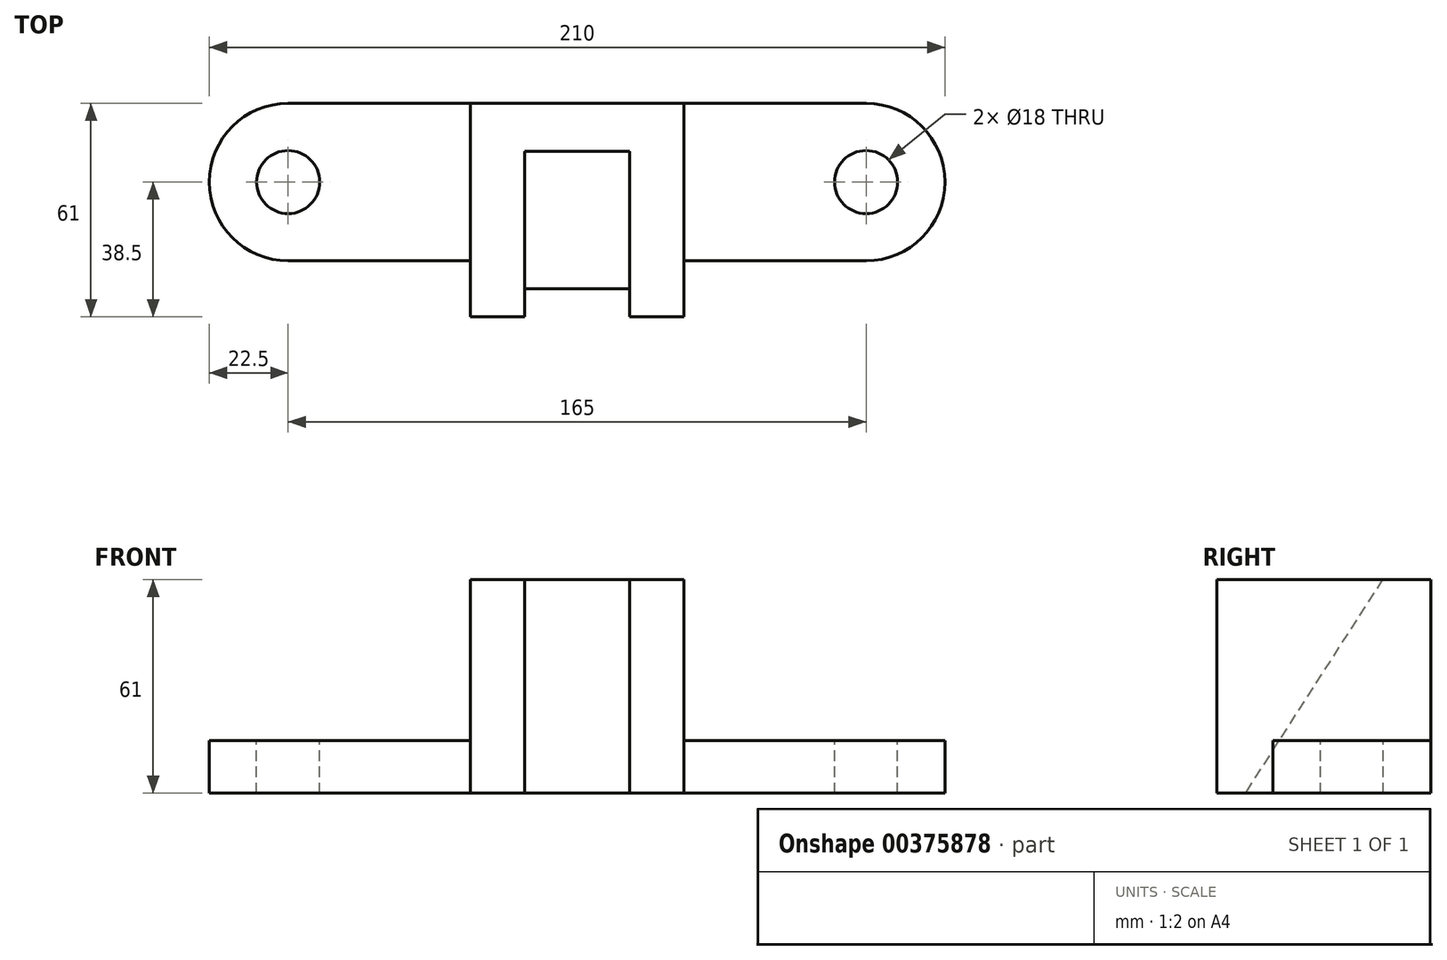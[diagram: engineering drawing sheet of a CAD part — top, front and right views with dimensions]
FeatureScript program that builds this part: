
annotation { "Feature Type Name" : "Feature", "Feature Type Description" : "" }
export const myFeature = defineFeature(function(context is Context, id is Id, definition is map)
    precondition{}
    {
        {
            var Q0;
            Q0=qCreatedBy(makeId("Front.planeOp"),FACE);
            var sketch = newSketch(context, id + "F0", { "sketchPlane" : qUnion([Q0])});
            skLineSegment(sketch, "E0.bottom", {"start": v(-30.5, 30.5) * mm, "end": v(30.5, 30.5) * mm});
            skLineSegment(sketch, "E0.top", {"start": v(-30.5, -30.5) * mm, "end": v(30.5, -30.5) * mm});
            skLineSegment(sketch, "E0.left", {"start": v(-30.5, 30.5) * mm, "end": v(-30.5, -30.5) * mm});
            skLineSegment(sketch, "E0.right", {"start": v(30.5, 30.5) * mm, "end": v(30.5, -30.5) * mm});
            skLineSegment(sketch, "E1.bottom", {"start": v(-30.5, -30.5) * mm, "end": v(-82.5, -30.5) * mm});
            skLineSegment(sketch, "E1.top", {"start": v(-30.5, -15.5) * mm, "end": v(-82.5, -15.5) * mm});
            skLineSegment(sketch, "E1.left", {"start": v(-30.5, -30.5) * mm, "end": v(-30.5, -15.5) * mm});
            skLineSegment(sketch, "E1.right", {"start": v(-82.5, -30.5) * mm, "end": v(-82.5, -15.5) * mm});
            skLineSegment(sketch, "E2.bottom", {"start": v(30.5, -30.5) * mm, "end": v(82.5, -30.5) * mm});
            skLineSegment(sketch, "E2.top", {"start": v(30.5, -15.5) * mm, "end": v(82.5, -15.5) * mm});
            skLineSegment(sketch, "E2.left", {"start": v(30.5, -30.5) * mm, "end": v(30.5, -15.5) * mm});
            skLineSegment(sketch, "E2.right", {"start": v(82.5, -30.5) * mm, "end": v(82.5, -15.5) * mm});
            skSolve(sketch);
        }
        {
            var Q0;
            Q0=makeQuery(id+"F0.imprint","IMPRINT",FACE,{"disambiguationData":[TD([[makeQuery(id+"F0.imprint","IMPRINT",EDGE,{"derivedFrom":sQuery(id+"F0.wireOp",EDGE,"E1.bottom")}),-1.0]])]});
            var Q1;
            Q1=makeQuery(id+"F0.imprint","IMPRINT",FACE,{"disambiguationData":[TD([[makeQuery(id+"F0.imprint","IMPRINT",EDGE,{"derivedFrom":sQuery(id+"F0.wireOp",EDGE,"E2.bottom")}),1.0]])]});
            extrude(context, id + "F1", {"entities" : qUnion([Q0, Q1]), "depth" : 45 * mm});
        }
        {
            var Q0;
            Q0=makeQuery(id+"F0.imprint","IMPRINT",FACE,{"disambiguationData":[TD([[makeQuery(id+"F0.imprint","IMPRINT",EDGE,{"derivedFrom":sQuery(id+"F0.wireOp",EDGE,"E0.bottom")}),-1.0]])]});
            extrude(context, id + "F2", {"entities" : qUnion([Q0]), "operationType" : NewBodyOperationType.ADD, "depth" : 61 * mm});
        }
        {
            var Q0;
            Q0=makeQuery(id+"F1.opExtrude","SWEPT_FACE",FACE,{"disambiguationData":[OSD([sQuery(id+"F0.wireOp",EDGE,"E1.top")])]});
            var sketch = newSketch(context, id + "F3", { "sketchPlane" : qUnion([Q0])});
            skCircle(sketch, "E3", {"center": v(-82.5, -22.5) * mm, "radius": 22.5 * mm});
            skLineSegment(sketch, "E4", {"start": v(-82.5, 0) * mm, "end": v(-82.5, -45) * mm});
            skArc(sketch, "E5", {"start": v(82.5, -45) * mm, "mid": v(105, -22.5) * mm, "end": v(82.5, 0) * mm});
            skLineSegment(sketch, "E6", {"start": v(82.5, 0) * mm, "end": v(82.5, -45) * mm});
            skSolve(sketch);
        }
        {
            var Q0;
            {var subQ0=sQuery(id+"F3.wireOp",EDGE,"E4");Q0=makeQuery(id+"F3.imprint","IMPRINT",FACE,{"disambiguationData":[TD([[makeQuery(id+"F3.imprint","IMPRINT",EDGE,{"derivedFrom":subQ0}),1.0]])]});}
            var Q1;
            Q1=makeQuery(id+"F3.imprint","IMPRINT",FACE,{"disambiguationData":[TD([[makeQuery(id+"F3.imprint","IMPRINT",EDGE,{"derivedFrom":sQuery(id+"F3.wireOp",EDGE,"E5")}),1.0]])]});
            extrude(context, id + "F4", {"entities" : qUnion([Q0, Q1]), "operationType" : NewBodyOperationType.ADD, "oppositeDirection" : true, "depth" : 15 * mm});
        }
        {
            var Q0;
            Q0=makeQuery(id+"F4.opExtrude","CAP_FACE",FACE,{"disambiguationData":[OSD([sQuery(id+"F3.wireOp",EDGE,"E3"),sQuery(id+"F3.wireOp",EDGE,"E4")])],"isStart":true});
            var sketch = newSketch(context, id + "F5", { "sketchPlane" : qUnion([Q0])});
            skCircle(sketch, "E7", {"center": v(-82.5, -22.5) * mm, "radius": 9 * mm});
            skSolve(sketch);
        }
        {
            var Q0;
            Q0=makeQuery(id+"F4.opExtrude","CAP_FACE",FACE,{"disambiguationData":[OSD([sQuery(id+"F3.wireOp",EDGE,"E5"),sQuery(id+"F3.wireOp",EDGE,"E6")])],"isStart":true});
            var sketch = newSketch(context, id + "F6", { "sketchPlane" : qUnion([Q0])});
            skCircle(sketch, "E8", {"center": v(82.5, -22.5) * mm, "radius": 9 * mm});
            skSolve(sketch);
        }
        {
            var Q0;
            Q0=makeQuery(id+"F6.imprint","IMPRINT",FACE,{"disambiguationData":[TD([[makeQuery(id+"F6.imprint","IMPRINT",EDGE,{"derivedFrom":sQuery(id+"F6.wireOp",EDGE,"E8")}),1.0]])]});
            var Q1;
            Q1=makeQuery(id+"F5.imprint","IMPRINT",FACE,{"disambiguationData":[TD([[makeQuery(id+"F5.imprint","IMPRINT",EDGE,{"derivedFrom":sQuery(id+"F5.wireOp",EDGE,"E7")}),1.0]])]});
            extrude(context, id + "F7", {"entities" : qUnion([Q0, Q1]), "operationType" : NewBodyOperationType.REMOVE, "oppositeDirection" : true, "depth" : 15 * mm});
        }
        {
            var Q0;
            Q0=makeQuery(id+"F2.opExtrude","SWEPT_FACE",FACE,{"disambiguationData":[OSD([sQuery(id+"F0.wireOp",EDGE,"E0.left"),sQuery(id+"F0.wireOp",EDGE,"E1.left")])]});
            cPlane(context, id + "F8", {"entities" : qUnion([Q0]), "cplaneType" : CPlaneType.OFFSET, "offset" : 15.5 * mm, "oppositeDirection" : true, "width" : 150 * mm, "height" : 150 * mm});
        }
        {
            var Q0;
            Q0=qCreatedBy(id+"F8.planeOp",FACE);
            var sketch = newSketch(context, id + "F9", { "sketchPlane" : qUnion([Q0])});
            skLineSegment(sketch, "E9", {"start": v(13.75, 30.5) * mm, "end": v(53, -30.5) * mm});
            skLineSegment(sketch, "E10", {"start": v(13.75, 30.5) * mm, "end": v(61, 30.5) * mm});
            skLineSegment(sketch, "E11", {"start": v(61, 30.5) * mm, "end": v(61, -30.5) * mm});
            skLineSegment(sketch, "E12", {"start": v(53, -30.5) * mm, "end": v(61, -30.5) * mm});
            skPoint(sketch, "E13.end.orphan", {"position": v(6, 30.5) * mm});
            skPoint(sketch, "E14.end.orphan", {"position": v(6, -30.5) * mm});
            skSolve(sketch);
        }
        {
            var Q0;
            Q0=qSketchRegion(id+"F9",true);
            extrude(context, id + "F10", {"entities" : qUnion([Q0]), "operationType" : NewBodyOperationType.REMOVE, "oppositeDirection" : true, "depth" : 30 * mm});
        }
    });
